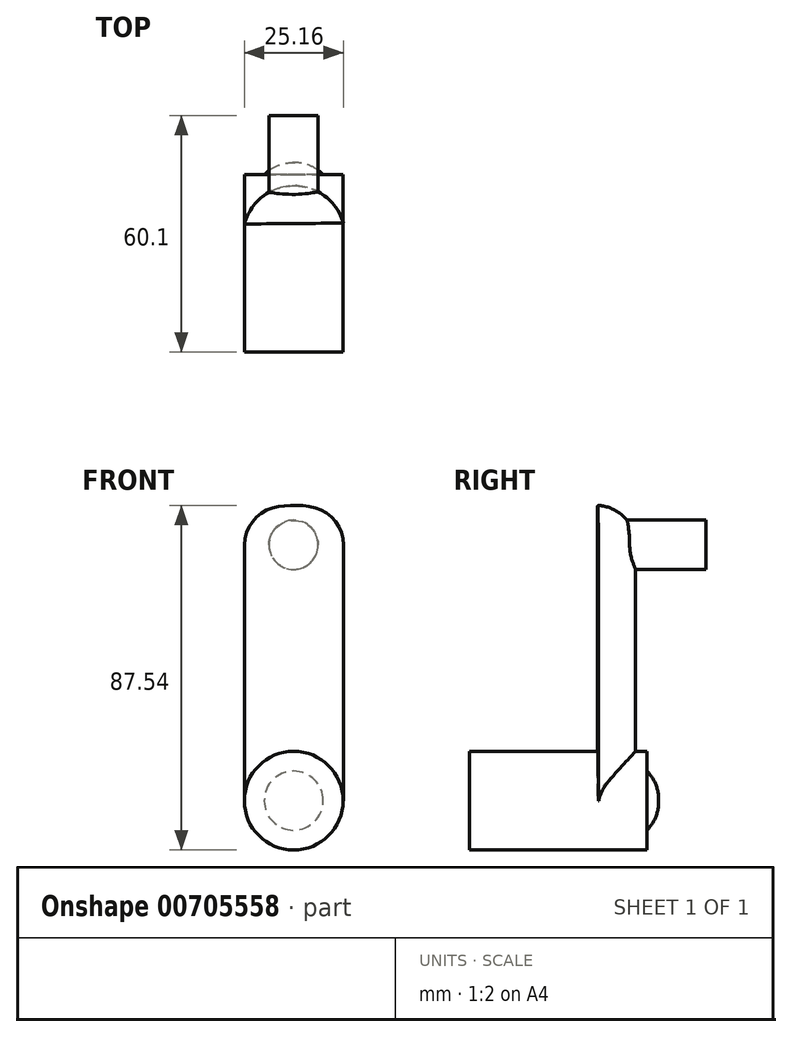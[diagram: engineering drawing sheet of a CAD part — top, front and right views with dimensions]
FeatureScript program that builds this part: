
annotation { "Feature Type Name" : "Feature", "Feature Type Description" : "" }
export const myFeature = defineFeature(function(context is Context, id is Id, definition is map)
    precondition{}
    {
        {
            var Q0;
            Q0=qCreatedBy(makeId("Front.planeOp"),FACE);
            var sketch = newSketch(context, id + "F0", { "sketchPlane" : qUnion([Q0])});
            skCircle(sketch, "E0", {"center": v(0, 0) * mm, "radius": 12.55 * mm});
            skSolve(sketch);
        }
        {
            var Q0;
            Q0=makeQuery(id+"F0.imprint","IMPRINT",FACE,{"disambiguationData":[TD([[makeQuery(id+"F0.imprint","IMPRINT",EDGE,{"derivedFrom":sQuery(id+"F0.wireOp",EDGE,"E0")}),1.0]])]});
            extrude(context, id + "F1", {"entities" : qUnion([Q0]), "depth" : 45.1 * mm, "offsetDistance" : 25 * mm});
        }
        {
            var Q0;
            Q0=qCreatedBy(makeId("Front.planeOp"),FACE);
            var sketch = newSketch(context, id + "F2", { "sketchPlane" : qUnion([Q0])});
            skCircle(sketch, "E1", {"center": v(0, 0) * mm, "radius": 7.5 * mm});
            skSolve(sketch);
        }
        {
            var Q0;
            Q0 = qSketchRegion(id + "F2", true);
            extrude(context, id + "F3", {"entities" : qUnion([Q0]), "operationType" : NewBodyOperationType.ADD, "oppositeDirection" : true, "depth" : 3 * mm, "offsetDistance" : 25 * mm});
        }
        {
            var Q0;
            Q0=makeQuery(id+"F3.opExtrude","CAP_FACE",FACE,{"disambiguationData":[OSD([sQuery(id+"F2.wireOp",EDGE,"E1")])],"isStart":false});
            fillet(context, id + "F4", {"entities" : qUnion([Q0]), "radius" : 10 * mm, "tangentPropagation" : true, "allowEdgeOverflow" : false});
        }
        {
            var Q0;
            Q0=qCreatedBy(makeId("Top.planeOp"),FACE);
            var sketch = newSketch(context, id + "F5", { "sketchPlane" : qUnion([Q0])});
            skArc(sketch, "E2", {"start": v(12.6, -12.34) * mm, "mid": v(-0.03, -2.85) * mm, "end": v(-12.5, -12.58) * mm});
            skLineSegment(sketch, "E3", {"start": v(-12.5, -12.58) * mm, "end": v(12.6, -12.34) * mm});
            skSolve(sketch);
        }
        {
            var Q0;
            Q0 = qSketchRegion(id + "F5", true);
            extrude(context, id + "F6", {"entities" : qUnion([Q0]), "operationType" : NewBodyOperationType.ADD, "depth" : 75 * mm, "offsetDistance" : 25 * mm});
        }
        {
            var Q0;
            Q0=makeQuery(id+"F6.opExtrude","CAP_EDGE",EDGE,{"disambiguationData":[OSD([sQuery(id+"F5.wireOp",EDGE,"E2")])],"isStart":false});
            fillet(context, id + "F7", {"entities" : qUnion([Q0]), "radius" : 10 * mm, "tangentPropagation" : true, "allowEdgeOverflow" : false});
        }
        {
            var Q0;
            Q0=qCreatedBy(makeId("Front.planeOp"),FACE);
            cPlane(context, id + "F8", {"entities" : qUnion([Q0]), "cplaneType" : CPlaneType.OFFSET, "offset" : 10 * mm, "width" : 150 * mm, "height" : 150 * mm});
        }
        {
            var Q0;
            Q0=qCreatedBy(id+"F8.planeOp",FACE);
            var sketch = newSketch(context, id + "F9", { "sketchPlane" : qUnion([Q0])});
            skCircle(sketch, "E4", {"center": v(-0.03, 65) * mm, "radius": 6.25 * mm});
            skSolve(sketch);
        }
        {
            var Q0;
            Q0 = qSketchRegion(id + "F9", true);
            extrude(context, id + "F10", {"entities" : qUnion([Q0]), "operationType" : NewBodyOperationType.ADD, "oppositeDirection" : true, "depth" : 25 * mm, "offsetDistance" : 25 * mm});
        }
    });
